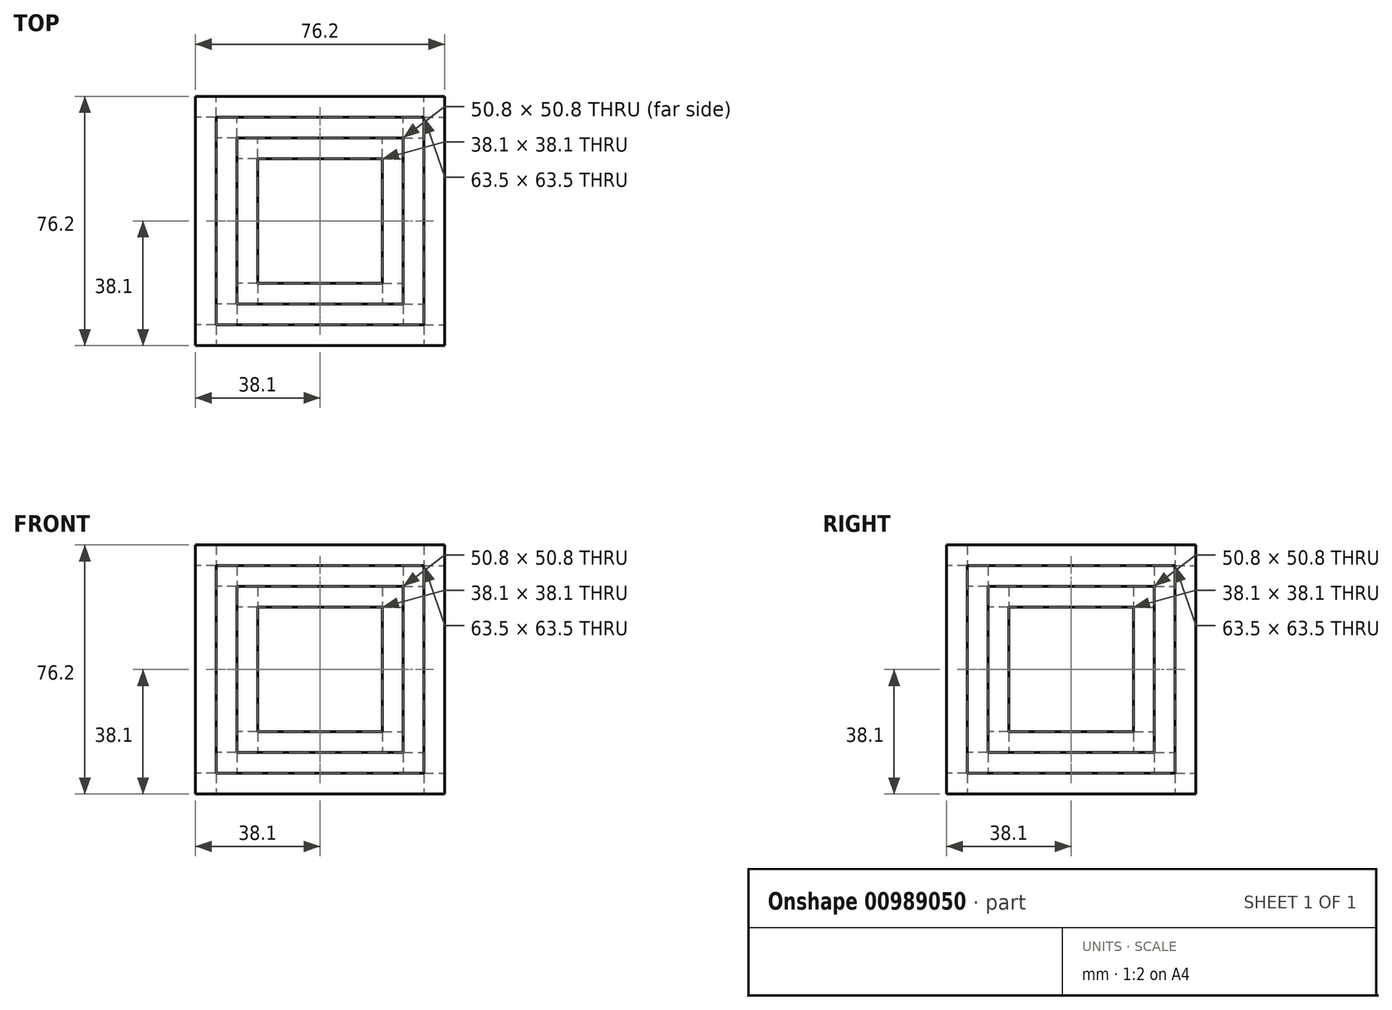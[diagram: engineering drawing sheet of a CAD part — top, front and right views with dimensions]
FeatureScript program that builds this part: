
annotation { "Feature Type Name" : "Feature", "Feature Type Description" : "" }
export const myFeature = defineFeature(function(context is Context, id is Id, definition is map)
    precondition{}
    {
        {
            var Q0;
            Q0=qCreatedBy(makeId("Top.planeOp"),FACE);
            var sketch = newSketch(context, id + "F0", { "sketchPlane" : qUnion([Q0])});
            skLineSegment(sketch, "E0.bottom", {"start": v(38.1, 38.1) * mm, "end": v(-38.1, 38.1) * mm});
            skLineSegment(sketch, "E0.top", {"start": v(38.1, -38.1) * mm, "end": v(-38.1, -38.1) * mm});
            skLineSegment(sketch, "E0.left", {"start": v(38.1, 38.1) * mm, "end": v(38.1, -38.1) * mm});
            skLineSegment(sketch, "E0.right", {"start": v(-38.1, 38.1) * mm, "end": v(-38.1, -38.1) * mm});
            skPoint(sketch, "E0.middle", {"position": v(0, 0) * mm});
            skLineSegment(sketch, "E1.0", {"start": v(31.75, 31.75) * mm, "end": v(-31.75, 31.75) * mm});
            skLineSegment(sketch, "E1.1", {"start": v(31.75, 31.75) * mm, "end": v(31.75, -31.75) * mm});
            skLineSegment(sketch, "E1.2", {"start": v(31.75, -31.75) * mm, "end": v(-31.75, -31.75) * mm});
            skLineSegment(sketch, "E1.3", {"start": v(-31.75, 31.75) * mm, "end": v(-31.75, -31.75) * mm});
            skSolve(sketch);
        }
        {
            var Q0;
            Q0=makeQuery(id+"F0.imprint","IMPRINT",FACE,{"disambiguationData":[TD([[makeQuery(id+"F0.imprint","IMPRINT",EDGE,{"derivedFrom":sQuery(id+"F0.wireOp",EDGE,"E0.bottom")}),1.0]])]});
            extrude(context, id + "F1", {"entities" : qUnion([Q0]), "depth" : 6.35 * mm, "offsetDistance" : 25.4 * mm});
        }
        {
            var Q0;
            Q0=makeQuery(id+"F1.opExtrude","CAP_FACE",FACE,{"disambiguationData":[OSD([sQuery(id+"F0.wireOp",EDGE,"E0.bottom"),sQuery(id+"F0.wireOp",EDGE,"E0.top"),sQuery(id+"F0.wireOp",EDGE,"E0.left"),sQuery(id+"F0.wireOp",EDGE,"E0.right"),sQuery(id+"F0.wireOp",EDGE,"E1.0"),sQuery(id+"F0.wireOp",EDGE,"E1.1"),sQuery(id+"F0.wireOp",EDGE,"E1.2"),sQuery(id+"F0.wireOp",EDGE,"E1.3")])],"isStart":false});
            var sketch = newSketch(context, id + "F2", { "sketchPlane" : qUnion([Q0])});
            skLineSegment(sketch, "E2.0", {"start": v(38.1, 38.1) * mm, "end": v(31.75, 38.1) * mm});
            skLineSegment(sketch, "E3.0", {"start": v(-38.1, 38.1) * mm, "end": v(-38.1, 31.75) * mm});
            skPoint(sketch, "E4.0", {"position": v(0, -31.75) * mm});
            skLineSegment(sketch, "E5.0", {"start": v(38.1, -38.1) * mm, "end": v(31.75, -38.1) * mm});
            skLineSegment(sketch, "E6.0", {"start": v(38.1, 38.1) * mm, "end": v(38.1, 31.75) * mm});
            skLineSegment(sketch, "E7", {"start": v(-31.75, 31.75) * mm, "end": v(-31.75, 38.1) * mm});
            skLineSegment(sketch, "E8", {"start": v(-31.75, 31.75) * mm, "end": v(-38.1, 31.75) * mm});
            skLineSegment(sketch, "E9", {"start": v(-31.75, -31.75) * mm, "end": v(-31.75, -38.1) * mm});
            skLineSegment(sketch, "E10", {"start": v(-31.75, -31.75) * mm, "end": v(-38.1, -31.75) * mm});
            skLineSegment(sketch, "E11", {"start": v(31.75, 31.75) * mm, "end": v(31.75, 38.1) * mm});
            skLineSegment(sketch, "E12", {"start": v(31.75, 31.75) * mm, "end": v(38.1, 31.75) * mm});
            skLineSegment(sketch, "E13", {"start": v(31.75, -31.75) * mm, "end": v(38.1, -31.75) * mm});
            skLineSegment(sketch, "E14", {"start": v(31.75, -31.75) * mm, "end": v(31.75, -38.1) * mm});
            skLineSegment(sketch, "E15.trimOffspring", {"start": v(-31.75, 38.1) * mm, "end": v(-38.1, 38.1) * mm});
            skLineSegment(sketch, "E16.trimOffspring", {"start": v(-38.1, -31.75) * mm, "end": v(-38.1, -38.1) * mm});
            skLineSegment(sketch, "E17.trimOffspring", {"start": v(-31.75, -38.1) * mm, "end": v(-38.1, -38.1) * mm});
            skLineSegment(sketch, "E18.trimOffspring", {"start": v(38.1, -31.75) * mm, "end": v(38.1, -38.1) * mm});
            skSolve(sketch);
        }
        {
            var Q0;
            Q0 = qSketchRegion(id + "F2", true);
            extrude(context, id + "F3", {"entities" : qUnion([Q0]), "operationType" : NewBodyOperationType.ADD, "depth" : 63.5 * mm, "offsetDistance" : 25.4 * mm});
        }
        {
            var Q0;
            Q0=makeQuery(id+"F3.opExtrude","CAP_FACE",FACE,{"disambiguationData":[OSD([sQuery(id+"F2.wireOp",EDGE,"E3.0"),sQuery(id+"F2.wireOp",EDGE,"E7"),sQuery(id+"F2.wireOp",EDGE,"E8"),sQuery(id+"F2.wireOp",EDGE,"E15.trimOffspring")])],"isStart":false});
            var sketch = newSketch(context, id + "F4", { "sketchPlane" : qUnion([Q0])});
            skLineSegment(sketch, "E19.0", {"start": v(38.1, 38.1) * mm, "end": v(-38.1, 38.1) * mm});
            skLineSegment(sketch, "E20.0", {"start": v(-38.1, 38.1) * mm, "end": v(-38.1, -38.1) * mm});
            skLineSegment(sketch, "E21.0", {"start": v(38.1, -38.1) * mm, "end": v(-38.1, -38.1) * mm});
            skLineSegment(sketch, "E22.0", {"start": v(38.1, 38.1) * mm, "end": v(38.1, -38.1) * mm});
            skLineSegment(sketch, "E23.0", {"start": v(31.75, 31.75) * mm, "end": v(-31.75, 31.75) * mm});
            skLineSegment(sketch, "E24.0", {"start": v(-31.75, 31.75) * mm, "end": v(-31.75, -31.75) * mm});
            skLineSegment(sketch, "E25.0", {"start": v(31.75, 31.75) * mm, "end": v(31.75, -31.75) * mm});
            skLineSegment(sketch, "E26.0", {"start": v(31.75, -31.75) * mm, "end": v(-31.75, -31.75) * mm});
            skSolve(sketch);
        }
        {
            var Q0;
            Q0 = qSketchRegion(id + "F4", true);
            extrude(context, id + "F5", {"entities" : qUnion([Q0]), "operationType" : NewBodyOperationType.ADD, "depth" : 6.35 * mm, "offsetDistance" : 25.4 * mm});
        }
        {
            var Q0;
            {var subQ0=sQuery(id+"F0.wireOp",EDGE,"E0.right");var subQ1=sQuery(id+"F0.wireOp",EDGE,"E1.3");var subQ2=sQuery(id+"F0.wireOp",EDGE,"E1.2");var subQ3=sQuery(id+"F0.wireOp",EDGE,"E1.0");var subQ4=makeQuery(id+"F1.opExtrude","CAP_FACE",FACE,{"disambiguationData":[OSD([sQuery(id+"F0.wireOp",EDGE,"E0.bottom"),sQuery(id+"F0.wireOp",EDGE,"E0.top"),sQuery(id+"F0.wireOp",EDGE,"E0.left"),subQ0,subQ3,sQuery(id+"F0.wireOp",EDGE,"E1.1"),subQ2,subQ1])],"isStart":false});Q0=makeQuery(id+"F3.boolean.opBoolean","SPLIT",FACE,{"disambiguationData":[TD([makeQuery(id+"F1.opExtrude","SWEPT_FACE",FACE,{"disambiguationData":[OSD([subQ0])]})])],"derivedFrom":subQ4});}
            var sketch = newSketch(context, id + "F6", { "sketchPlane" : qUnion([Q0])});
            skLineSegment(sketch, "E27.0", {"start": v(-31.75, 31.75) * mm, "end": v(-31.75, -31.75) * mm});
            skLineSegment(sketch, "E28.0", {"start": v(31.75, 31.75) * mm, "end": v(-31.75, 31.75) * mm});
            skLineSegment(sketch, "E29.0", {"start": v(31.75, 31.75) * mm, "end": v(31.75, -31.75) * mm});
            skLineSegment(sketch, "E30.0", {"start": v(31.75, -31.75) * mm, "end": v(-31.75, -31.75) * mm});
            skLineSegment(sketch, "E31.0", {"start": v(25.4, 25.4) * mm, "end": v(-25.4, 25.4) * mm});
            skLineSegment(sketch, "E31.1", {"start": v(25.4, 25.4) * mm, "end": v(25.4, -25.4) * mm});
            skLineSegment(sketch, "E31.2", {"start": v(25.4, -25.4) * mm, "end": v(-25.4, -25.4) * mm});
            skLineSegment(sketch, "E31.3", {"start": v(-25.4, 25.4) * mm, "end": v(-25.4, -25.4) * mm});
            skSolve(sketch);
        }
        {
            var Q0;
            Q0 = qSketchRegion(id + "F6", true);
            extrude(context, id + "F7", {"entities" : qUnion([Q0]), "depth" : 6.35 * mm, "offsetDistance" : 25.4 * mm});
        }
        {
            var Q0;
            Q0=makeQuery(id+"F7.opExtrude","CAP_FACE",FACE,{"disambiguationData":[OSD([sQuery(id+"F6.wireOp",EDGE,"E27.0"),sQuery(id+"F6.wireOp",EDGE,"E28.0"),sQuery(id+"F6.wireOp",EDGE,"E29.0"),sQuery(id+"F6.wireOp",EDGE,"E30.0"),sQuery(id+"F6.wireOp",EDGE,"E31.0"),sQuery(id+"F6.wireOp",EDGE,"E31.1"),sQuery(id+"F6.wireOp",EDGE,"E31.2"),sQuery(id+"F6.wireOp",EDGE,"E31.3")])],"isStart":false});
            var sketch = newSketch(context, id + "F8", { "sketchPlane" : qUnion([Q0])});
            skLineSegment(sketch, "E32.bottom", {"start": v(-25.4, 25.4) * mm, "end": v(-31.75, 25.4) * mm});
            skLineSegment(sketch, "E32.top", {"start": v(-25.4, 31.75) * mm, "end": v(-31.75, 31.75) * mm});
            skLineSegment(sketch, "E32.left", {"start": v(-25.4, 25.4) * mm, "end": v(-25.4, 31.75) * mm});
            skLineSegment(sketch, "E32.right", {"start": v(-31.75, 25.4) * mm, "end": v(-31.75, 31.75) * mm});
            skLineSegment(sketch, "E33.bottom", {"start": v(25.4, 25.4) * mm, "end": v(31.75, 25.4) * mm});
            skLineSegment(sketch, "E33.top", {"start": v(25.4, 31.75) * mm, "end": v(31.75, 31.75) * mm});
            skLineSegment(sketch, "E33.left", {"start": v(25.4, 25.4) * mm, "end": v(25.4, 31.75) * mm});
            skLineSegment(sketch, "E33.right", {"start": v(31.75, 25.4) * mm, "end": v(31.75, 31.75) * mm});
            skLineSegment(sketch, "E34.bottom", {"start": v(25.4, -25.4) * mm, "end": v(31.75, -25.4) * mm});
            skLineSegment(sketch, "E34.top", {"start": v(25.4, -31.75) * mm, "end": v(31.75, -31.75) * mm});
            skLineSegment(sketch, "E34.left", {"start": v(25.4, -25.4) * mm, "end": v(25.4, -31.75) * mm});
            skLineSegment(sketch, "E34.right", {"start": v(31.75, -25.4) * mm, "end": v(31.75, -31.75) * mm});
            skLineSegment(sketch, "E35.bottom", {"start": v(-25.4, -25.4) * mm, "end": v(-31.75, -25.4) * mm});
            skLineSegment(sketch, "E35.top", {"start": v(-25.4, -31.75) * mm, "end": v(-31.75, -31.75) * mm});
            skLineSegment(sketch, "E35.left", {"start": v(-25.4, -25.4) * mm, "end": v(-25.4, -31.75) * mm});
            skLineSegment(sketch, "E35.right", {"start": v(-31.75, -25.4) * mm, "end": v(-31.75, -31.75) * mm});
            skSolve(sketch);
        }
        {
            var Q0;
            Q0 = qSketchRegion(id + "F8", true);
            extrude(context, id + "F9", {"entities" : qUnion([Q0]), "operationType" : NewBodyOperationType.ADD, "depth" : 50.8 * mm, "offsetDistance" : 25.4 * mm});
        }
        {
            var Q0;
            Q0=makeQuery(id+"F9.opExtrude","CAP_FACE",FACE,{"disambiguationData":[OSD([sQuery(id+"F8.wireOp",EDGE,"E35.bottom"),sQuery(id+"F8.wireOp",EDGE,"E35.top"),sQuery(id+"F8.wireOp",EDGE,"E35.left"),sQuery(id+"F8.wireOp",EDGE,"E35.right")])],"isStart":false});
            var sketch = newSketch(context, id + "F10", { "sketchPlane" : qUnion([Q0])});
            skLineSegment(sketch, "E36.0", {"start": v(25.4, -25.4) * mm, "end": v(-25.4, -25.4) * mm});
            skLineSegment(sketch, "E36.1", {"start": v(-25.4, 25.4) * mm, "end": v(-25.4, -25.4) * mm});
            skLineSegment(sketch, "E36.2", {"start": v(25.4, 25.4) * mm, "end": v(-25.4, 25.4) * mm});
            skLineSegment(sketch, "E36.3", {"start": v(25.4, 25.4) * mm, "end": v(25.4, -25.4) * mm});
            skLineSegment(sketch, "E36.4", {"start": v(31.75, 31.75) * mm, "end": v(31.75, -31.75) * mm});
            skLineSegment(sketch, "E36.5", {"start": v(31.75, -31.75) * mm, "end": v(-31.75, -31.75) * mm});
            skLineSegment(sketch, "E36.6", {"start": v(-31.75, 31.75) * mm, "end": v(-31.75, -31.75) * mm});
            skLineSegment(sketch, "E36.7", {"start": v(31.75, 31.75) * mm, "end": v(-31.75, 31.75) * mm});
            skSolve(sketch);
        }
        {
            var Q0;
            Q0 = qSketchRegion(id + "F10", true);
            extrude(context, id + "F11", {"entities" : qUnion([Q0]), "operationType" : NewBodyOperationType.ADD, "depth" : 6.35 * mm, "offsetDistance" : 25.4 * mm});
        }
        {
            var Q0;
            {var subQ0=sQuery(id+"F6.wireOp",EDGE,"E31.1");var subQ1=sQuery(id+"F6.wireOp",EDGE,"E31.3");var subQ2=sQuery(id+"F6.wireOp",EDGE,"E31.0");var subQ3=sQuery(id+"F6.wireOp",EDGE,"E28.0");var subQ4=makeQuery(id+"F7.opExtrude","CAP_FACE",FACE,{"disambiguationData":[OSD([sQuery(id+"F6.wireOp",EDGE,"E27.0"),subQ3,sQuery(id+"F6.wireOp",EDGE,"E29.0"),sQuery(id+"F6.wireOp",EDGE,"E30.0"),subQ2,subQ0,sQuery(id+"F6.wireOp",EDGE,"E31.2"),subQ1])],"isStart":false});Q0=makeQuery(id+"F9.boolean.opBoolean","SPLIT",FACE,{"disambiguationData":[TD([makeQuery(id+"F7.opExtrude","SWEPT_FACE",FACE,{"disambiguationData":[OSD([subQ3])]})])],"derivedFrom":subQ4});}
            var sketch = newSketch(context, id + "F12", { "sketchPlane" : qUnion([Q0])});
            skLineSegment(sketch, "E37.0", {"start": v(25.4, 25.4) * mm, "end": v(-25.4, 25.4) * mm});
            skLineSegment(sketch, "E37.1", {"start": v(-25.4, 25.4) * mm, "end": v(-25.4, -25.4) * mm});
            skLineSegment(sketch, "E37.2", {"start": v(25.4, -25.4) * mm, "end": v(-25.4, -25.4) * mm});
            skLineSegment(sketch, "E37.3", {"start": v(25.4, 25.4) * mm, "end": v(25.4, -25.4) * mm});
            skLineSegment(sketch, "E38.0", {"start": v(19.05, 19.05) * mm, "end": v(-19.05, 19.05) * mm});
            skLineSegment(sketch, "E38.1", {"start": v(19.05, 19.05) * mm, "end": v(19.05, -19.05) * mm});
            skLineSegment(sketch, "E38.2", {"start": v(19.05, -19.05) * mm, "end": v(-19.05, -19.05) * mm});
            skLineSegment(sketch, "E38.3", {"start": v(-19.05, 19.05) * mm, "end": v(-19.05, -19.05) * mm});
            skSolve(sketch);
        }
        {
            var Q0;
            Q0 = qSketchRegion(id + "F12", true);
            extrude(context, id + "F13", {"entities" : qUnion([Q0]), "depth" : 6.35 * mm, "offsetDistance" : 25.4 * mm});
        }
        {
            var Q0;
            Q0=makeQuery(id+"F13.opExtrude","CAP_FACE",FACE,{"disambiguationData":[OSD([sQuery(id+"F12.wireOp",EDGE,"E37.0"),sQuery(id+"F12.wireOp",EDGE,"E37.1"),sQuery(id+"F12.wireOp",EDGE,"E37.2"),sQuery(id+"F12.wireOp",EDGE,"E37.3"),sQuery(id+"F12.wireOp",EDGE,"E38.0"),sQuery(id+"F12.wireOp",EDGE,"E38.1"),sQuery(id+"F12.wireOp",EDGE,"E38.2"),sQuery(id+"F12.wireOp",EDGE,"E38.3")])],"isStart":false});
            var sketch = newSketch(context, id + "F14", { "sketchPlane" : qUnion([Q0])});
            skLineSegment(sketch, "E39.bottom", {"start": v(-19.05, 19.05) * mm, "end": v(-25.4, 19.05) * mm});
            skLineSegment(sketch, "E39.top", {"start": v(-19.05, 25.4) * mm, "end": v(-25.4, 25.4) * mm});
            skLineSegment(sketch, "E39.left", {"start": v(-19.05, 19.05) * mm, "end": v(-19.05, 25.4) * mm});
            skLineSegment(sketch, "E39.right", {"start": v(-25.4, 19.05) * mm, "end": v(-25.4, 25.4) * mm});
            skLineSegment(sketch, "E40.bottom", {"start": v(19.05, 19.05) * mm, "end": v(25.4, 19.05) * mm});
            skLineSegment(sketch, "E40.top", {"start": v(19.05, 25.4) * mm, "end": v(25.4, 25.4) * mm});
            skLineSegment(sketch, "E40.left", {"start": v(19.05, 19.05) * mm, "end": v(19.05, 25.4) * mm});
            skLineSegment(sketch, "E40.right", {"start": v(25.4, 19.05) * mm, "end": v(25.4, 25.4) * mm});
            skLineSegment(sketch, "E41.bottom", {"start": v(19.05, -19.05) * mm, "end": v(25.4, -19.05) * mm});
            skLineSegment(sketch, "E41.top", {"start": v(19.05, -25.4) * mm, "end": v(25.4, -25.4) * mm});
            skLineSegment(sketch, "E41.left", {"start": v(19.05, -19.05) * mm, "end": v(19.05, -25.4) * mm});
            skLineSegment(sketch, "E41.right", {"start": v(25.4, -19.05) * mm, "end": v(25.4, -25.4) * mm});
            skLineSegment(sketch, "E42.bottom", {"start": v(-19.05, -19.05) * mm, "end": v(-25.4, -19.05) * mm});
            skLineSegment(sketch, "E42.top", {"start": v(-19.05, -25.4) * mm, "end": v(-25.4, -25.4) * mm});
            skLineSegment(sketch, "E42.left", {"start": v(-19.05, -19.05) * mm, "end": v(-19.05, -25.4) * mm});
            skLineSegment(sketch, "E42.right", {"start": v(-25.4, -19.05) * mm, "end": v(-25.4, -25.4) * mm});
            skSolve(sketch);
        }
        {
            var Q0;
            Q0 = qSketchRegion(id + "F14", true);
            extrude(context, id + "F15", {"entities" : qUnion([Q0]), "operationType" : NewBodyOperationType.ADD, "depth" : 38.1 * mm, "offsetDistance" : 25.4 * mm});
        }
        {
            var Q0;
            Q0=makeQuery(id+"F15.opExtrude","CAP_FACE",FACE,{"disambiguationData":[OSD([sQuery(id+"F14.wireOp",EDGE,"E39.bottom"),sQuery(id+"F14.wireOp",EDGE,"E39.top"),sQuery(id+"F14.wireOp",EDGE,"E39.left"),sQuery(id+"F14.wireOp",EDGE,"E39.right")])],"isStart":false});
            var sketch = newSketch(context, id + "F16", { "sketchPlane" : qUnion([Q0])});
            skLineSegment(sketch, "E43.0", {"start": v(-19.05, 19.05) * mm, "end": v(-19.05, -19.05) * mm});
            skLineSegment(sketch, "E43.1", {"start": v(-25.4, 25.4) * mm, "end": v(-25.4, -25.4) * mm});
            skLineSegment(sketch, "E43.2", {"start": v(19.05, -19.05) * mm, "end": v(-19.05, -19.05) * mm});
            skLineSegment(sketch, "E43.3", {"start": v(25.4, -25.4) * mm, "end": v(-25.4, -25.4) * mm});
            skLineSegment(sketch, "E43.4", {"start": v(19.05, 19.05) * mm, "end": v(-19.05, 19.05) * mm});
            skLineSegment(sketch, "E43.5", {"start": v(19.05, 19.05) * mm, "end": v(19.05, -19.05) * mm});
            skLineSegment(sketch, "E43.6", {"start": v(25.4, 25.4) * mm, "end": v(25.4, -25.4) * mm});
            skLineSegment(sketch, "E43.7", {"start": v(25.4, 25.4) * mm, "end": v(-25.4, 25.4) * mm});
            skSolve(sketch);
        }
        {
            var Q0;
            Q0 = qSketchRegion(id + "F16", true);
            extrude(context, id + "F17", {"entities" : qUnion([Q0]), "operationType" : NewBodyOperationType.ADD, "depth" : 6.35 * mm, "offsetDistance" : 25.4 * mm});
        }
    });
